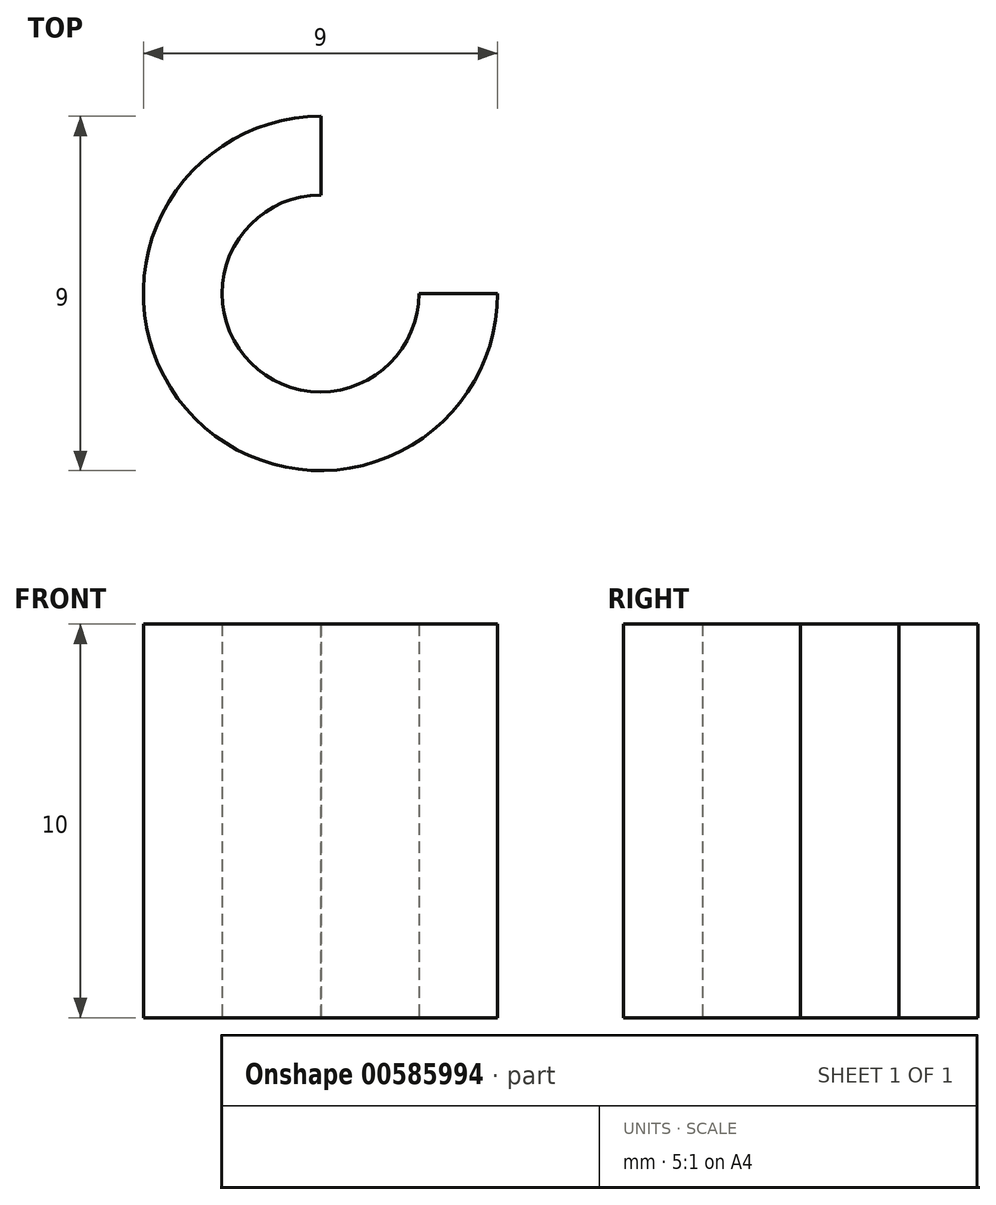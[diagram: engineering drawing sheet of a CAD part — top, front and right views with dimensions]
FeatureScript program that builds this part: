
annotation { "Feature Type Name" : "Feature", "Feature Type Description" : "" }
export const myFeature = defineFeature(function(context is Context, id is Id, definition is map)
    precondition{}
    {
        {
            var Q0;
            Q0=qCreatedBy(makeId("Top.planeOp"),FACE);
            var sketch = newSketch(context, id + "F0", { "sketchPlane" : qUnion([Q0])});
            skCircle(sketch, "E0", {"center": v(0, 0) * mm, "radius": 2.5 * mm});
            skCircle(sketch, "E1", {"center": v(0, 0) * mm, "radius": 4.5 * mm});
            skLineSegment(sketch, "E2", {"start": v(2.5, 0) * mm, "end": v(0, 2.5) * mm});
            skLineSegment(sketch, "E3.bottom", {"start": v(0, 2.5) * mm, "end": v(2.5, 2.5) * mm});
            skLineSegment(sketch, "E3.top", {"start": v(0, 0) * mm, "end": v(2.5, 0) * mm});
            skLineSegment(sketch, "E3.left", {"start": v(0, 2.5) * mm, "end": v(0, 0) * mm});
            skLineSegment(sketch, "E3.right", {"start": v(2.5, 2.5) * mm, "end": v(2.5, 0) * mm});
            skLineSegment(sketch, "E4.bottom", {"start": v(4.99, 0) * mm, "end": v(0.01, 0) * mm});
            skLineSegment(sketch, "E4.top", {"start": v(4.99, 5) * mm, "end": v(0.01, 5) * mm});
            skLineSegment(sketch, "E4.left", {"start": v(4.99, 0) * mm, "end": v(4.99, 5) * mm});
            skLineSegment(sketch, "E4.right", {"start": v(0.01, 0) * mm, "end": v(0.01, 5) * mm});
            skPoint(sketch, "E4.middle", {"position": v(2.5, 2.5) * mm});
            skSolve(sketch);
        }
        {
            var Q0;
            {var subQ0=sQuery(id+"F0.wireOp",EDGE,"E4.bottom");var subQ4=sQuery(id+"F0.wireOp",EDGE,"E1");var subQ5=makeQuery(id+"F0.imprint","INTERSECT",VERTEX,{"derivedFrom":[subQ4,subQ0]});Q0=makeQuery(id+"F0.imprint","IMPRINT",FACE,{"disambiguationData":[TD([[makeQuery(id+"F0.imprint","IMPRINT",EDGE,{"disambiguationData":[TD([[subQ5,1.0]])],"derivedFrom":subQ4}),1.0]])]});}
            extrude(context, id + "F1", {"entities" : qUnion([Q0]), "depth" : 10 * mm, "offsetDistance" : 25 * mm});
        }
    });
